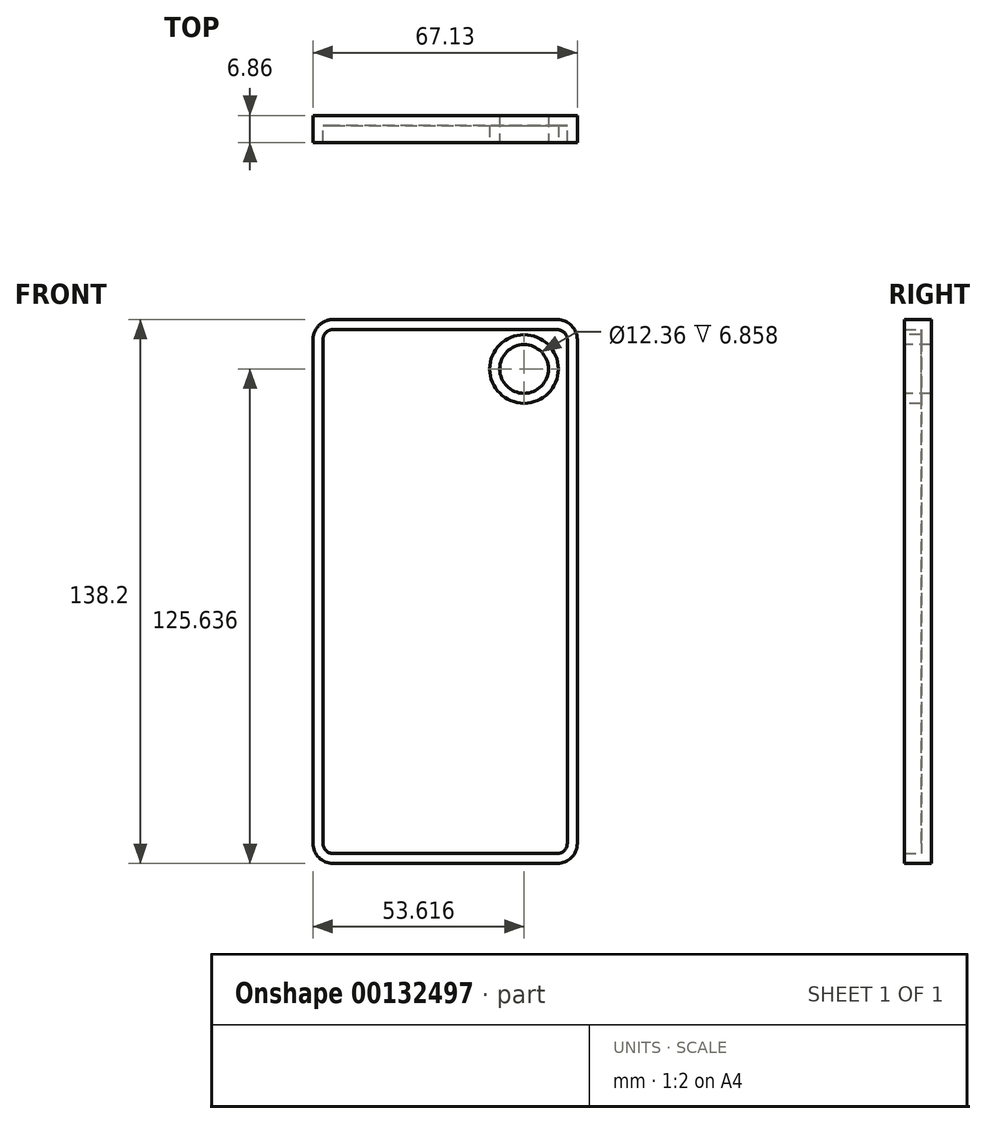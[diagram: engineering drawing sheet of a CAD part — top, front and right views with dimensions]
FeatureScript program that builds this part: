
annotation { "Feature Type Name" : "Feature", "Feature Type Description" : "" }
export const myFeature = defineFeature(function(context is Context, id is Id, definition is map)
    precondition{}
    {
        {
            var Q0;
            Q0=qCreatedBy(makeId("Front.planeOp"),FACE);
            var sketch = newSketch(context, id + "F0", { "sketchPlane" : qUnion([Q0])});
            skLineSegment(sketch, "E0", {"start": v(0, 76.25) * mm, "end": v(0, -61.93) * mm});
            skLineSegment(sketch, "E1", {"start": v(0, -61.93) * mm, "end": v(-67.13, -61.93) * mm});
            skLineSegment(sketch, "E2", {"start": v(-67.13, -61.93) * mm, "end": v(-67.13, 76.27) * mm});
            skLineSegment(sketch, "E3", {"start": v(-67.13, 76.27) * mm, "end": v(0, 76.25) * mm});
            skSolve(sketch);
        }
        {
            var Q0;
            Q0=makeQuery(id+"F0.imprint","IMPRINT",FACE,{"disambiguationData":[TD([[makeQuery(id+"F0.imprint","IMPRINT",EDGE,{"derivedFrom":sQuery(id+"F0.wireOp",EDGE,"E0")}),-1.0]])]});
            extrude(context, id + "F1", {"entities" : qUnion([Q0]), "depth" : 6.86 * mm});
        }
        {
            var Q0;
            Q0=makeQuery(id+"F1.opExtrude","SWEPT_EDGE",EDGE,{"disambiguationData":[OSD([sQuery(id+"F0.wireOp",EDGE,"E2"),sQuery(id+"F0.wireOp",EDGE,"E3")])]});
            var Q1;
            Q1=makeQuery(id+"F1.opExtrude","SWEPT_EDGE",EDGE,{"disambiguationData":[OSD([sQuery(id+"F0.wireOp",EDGE,"E0"),sQuery(id+"F0.wireOp",EDGE,"E1")])]});
            var Q2;
            Q2=makeQuery(id+"F1.opExtrude","SWEPT_EDGE",EDGE,{"disambiguationData":[OSD([sQuery(id+"F0.wireOp",EDGE,"E1"),sQuery(id+"F0.wireOp",EDGE,"E2")])]});
            var Q3;
            Q3=makeQuery(id+"F1.opExtrude","SWEPT_EDGE",EDGE,{"disambiguationData":[OSD([sQuery(id+"F0.wireOp",EDGE,"E0"),sQuery(id+"F0.wireOp",EDGE,"E3")])]});
            fillet(context, id + "F2", {"entities" : qUnion([Q0, Q1, Q2, Q3]), "radius" : 5.08 * mm, "tangentPropagation" : true, "allowEdgeOverflow" : false});
        }
        {
            var Q0;
            Q0=makeQuery(id+"F1.opExtrude","CAP_FACE",FACE,{"disambiguationData":[OSD([sQuery(id+"F0.wireOp",EDGE,"E0"),sQuery(id+"F0.wireOp",EDGE,"E1"),sQuery(id+"F0.wireOp",EDGE,"E2"),sQuery(id+"F0.wireOp",EDGE,"E3")])],"isStart":false});
            var sketch = newSketch(context, id + "F3", { "sketchPlane" : qUnion([Q0])});
            skCircle(sketch, "E4", {"center": v(-13.51, 63.7) * mm, "radius": 6.18 * mm});
            skSolve(sketch);
        }
        {
            var Q0;
            Q0=makeQuery(id+"F3.imprint","IMPRINT",FACE,{"disambiguationData":[TD([[makeQuery(id+"F3.imprint","IMPRINT",EDGE,{"derivedFrom":sQuery(id+"F3.wireOp",EDGE,"E4")}),1.0]])]});
            extrude(context, id + "F4", {"entities" : qUnion([Q0]), "operationType" : NewBodyOperationType.REMOVE, "oppositeDirection" : true, "depth" : 6.86 * mm});
        }
        {
            var Q0;
            Q0=makeQuery(id+"F1.opExtrude","CAP_FACE",FACE,{"disambiguationData":[OSD([sQuery(id+"F0.wireOp",EDGE,"E0"),sQuery(id+"F0.wireOp",EDGE,"E1"),sQuery(id+"F0.wireOp",EDGE,"E2"),sQuery(id+"F0.wireOp",EDGE,"E3")])],"isStart":false});
            var sketch = newSketch(context, id + "F5", { "sketchPlane" : qUnion([Q0])});
            skSolve(sketch);
        }
        {
            var Q0;
            Q0=makeQuery(id+"F1.opExtrude","CAP_FACE",FACE,{"disambiguationData":[OSD([sQuery(id+"F0.wireOp",EDGE,"E0"),sQuery(id+"F0.wireOp",EDGE,"E1"),sQuery(id+"F0.wireOp",EDGE,"E2"),sQuery(id+"F0.wireOp",EDGE,"E3")])],"isStart":false});
            shell(context, id + "F6", {"entities" : qUnion([Q0]), "thickness" : 2.54 * mm});
        }
    });
